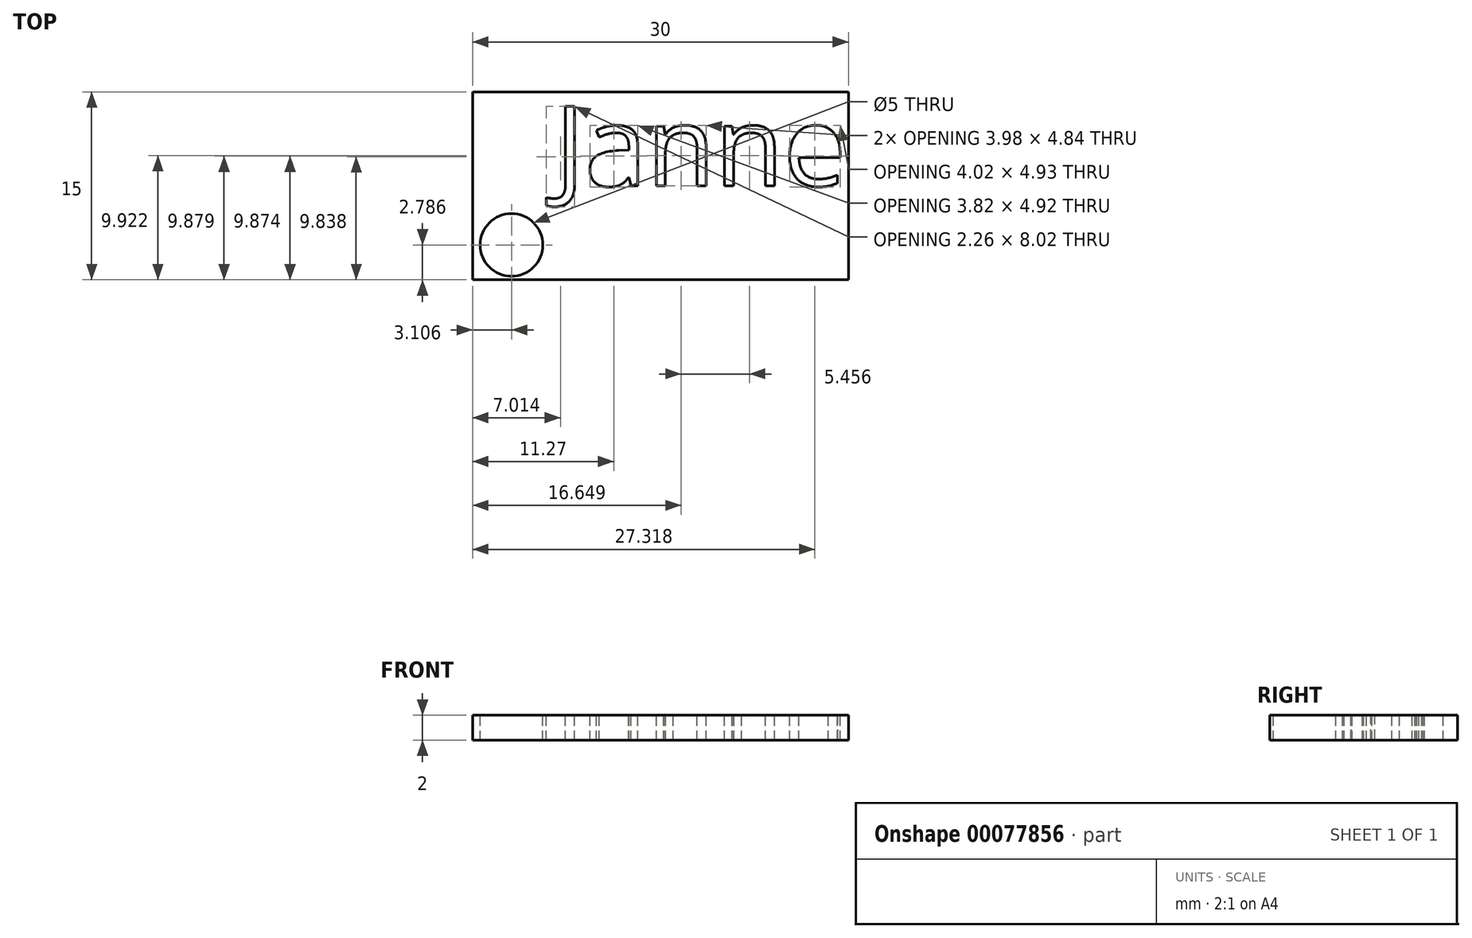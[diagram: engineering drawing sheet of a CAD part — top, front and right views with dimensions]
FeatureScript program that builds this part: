
annotation { "Feature Type Name" : "Feature", "Feature Type Description" : "" }
export const myFeature = defineFeature(function(context is Context, id is Id, definition is map)
    precondition{}
    {
        {
            var Q0;
            Q0=qCreatedBy(makeId("Top.planeOp"),FACE);
            var Q1;
            Q1=qCreatedBy(makeId("Top.planeOp"),FACE);
            var sketch = newSketch(context, id + "F0", { "sketchPlane" : qUnion([Q0, Q1])});
            skLineSegment(sketch, "E0", {"start": v(0, 0) * mm, "end": v(-30, 0) * mm});
            skLineSegment(sketch, "E1", {"start": v(-30, 0) * mm, "end": v(-30, 15) * mm});
            skLineSegment(sketch, "E2", {"start": v(-30, 15) * mm, "end": v(0, 15) * mm});
            skLineSegment(sketch, "E3", {"start": v(0, 15) * mm, "end": v(0, 0) * mm});
            skText(sketch, "E4", { "text": "Janne", "fontName": "OpenSans-Regular.ttf"});
            const initialGuessF0  = {"E4": [-0.02342, 0.0075, 1, 0, 0.0064]};
            skSetInitialGuess(sketch, initialGuessF0);
            skSolve(sketch);
        }
        {
            var Q0;
            Q0=makeQuery(id+"F0.imprint","IMPRINT",FACE,{"disambiguationData":[TD([[makeQuery(id+"F0.imprint","IMPRINT",EDGE,{"derivedFrom":sQuery(id+"F0.wireOp",EDGE,"E0")}),-1.0]])]});
            extrude(context, id + "F1", {"entities" : qUnion([Q0]), "oppositeDirection" : true, "depth" : 2 * mm});
        }
        {
            var Q0;
            Q0=makeQuery(id+"F1.opExtrude","CAP_FACE",FACE,{"disambiguationData":[OSD([sQuery(id+"F0.wireOp",EDGE,"E0"),sQuery(id+"F0.wireOp",EDGE,"E1"),sQuery(id+"F0.wireOp",EDGE,"E2"),sQuery(id+"F0.wireOp",EDGE,"E3"),sQuery(id+"F0.wireOp",EDGE,"E4.sketch_text.stroke-0"),sQuery(id+"F0.wireOp",EDGE,"E4.sketch_text.stroke-1"),sQuery(id+"F0.wireOp",EDGE,"E4.sketch_text.stroke-2"),sQuery(id+"F0.wireOp",EDGE,"E4.sketch_text.stroke-3"),sQuery(id+"F0.wireOp",EDGE,"E4.sketch_text.stroke-4"),sQuery(id+"F0.wireOp",EDGE,"E4.sketch_text.stroke-5"),sQuery(id+"F0.wireOp",EDGE,"E4.sketch_text.stroke-6"),sQuery(id+"F0.wireOp",EDGE,"E4.sketch_text.stroke-7"),sQuery(id+"F0.wireOp",EDGE,"E4.sketch_text.stroke-8"),sQuery(id+"F0.wireOp",EDGE,"E4.sketch_text.stroke-9"),sQuery(id+"F0.wireOp",EDGE,"E4.sketch_text.stroke-10"),sQuery(id+"F0.wireOp",EDGE,"E4.sketch_text.stroke-11"),sQuery(id+"F0.wireOp",EDGE,"E4.sketch_text.stroke-12"),sQuery(id+"F0.wireOp",EDGE,"E4.sketch_text.stroke-13"),sQuery(id+"F0.wireOp",EDGE,"E4.sketch_text.stroke-14"),sQuery(id+"F0.wireOp",EDGE,"E4.sketch_text.stroke-15"),sQuery(id+"F0.wireOp",EDGE,"E4.sketch_text.stroke-16"),sQuery(id+"F0.wireOp",EDGE,"E4.sketch_text.stroke-17"),sQuery(id+"F0.wireOp",EDGE,"E4.sketch_text.stroke-18"),sQuery(id+"F0.wireOp",EDGE,"E4.sketch_text.stroke-19"),sQuery(id+"F0.wireOp",EDGE,"E4.sketch_text.stroke-20"),sQuery(id+"F0.wireOp",EDGE,"E4.sketch_text.stroke-21"),sQuery(id+"F0.wireOp",EDGE,"E4.sketch_text.stroke-22"),sQuery(id+"F0.wireOp",EDGE,"E4.sketch_text.stroke-23"),sQuery(id+"F0.wireOp",EDGE,"E4.sketch_text.stroke-24"),sQuery(id+"F0.wireOp",EDGE,"E4.sketch_text.stroke-25"),sQuery(id+"F0.wireOp",EDGE,"E4.sketch_text.stroke-26"),sQuery(id+"F0.wireOp",EDGE,"E4.sketch_text.stroke-27"),sQuery(id+"F0.wireOp",EDGE,"E4.sketch_text.stroke-28"),sQuery(id+"F0.wireOp",EDGE,"E4.sketch_text.stroke-37"),sQuery(id+"F0.wireOp",EDGE,"E4.sketch_text.stroke-38"),sQuery(id+"F0.wireOp",EDGE,"E4.sketch_text.stroke-39"),sQuery(id+"F0.wireOp",EDGE,"E4.sketch_text.stroke-40"),sQuery(id+"F0.wireOp",EDGE,"E4.sketch_text.stroke-41"),sQuery(id+"F0.wireOp",EDGE,"E4.sketch_text.stroke-42"),sQuery(id+"F0.wireOp",EDGE,"E4.sketch_text.stroke-43"),sQuery(id+"F0.wireOp",EDGE,"E4.sketch_text.stroke-44"),sQuery(id+"F0.wireOp",EDGE,"E4.sketch_text.stroke-45"),sQuery(id+"F0.wireOp",EDGE,"E4.sketch_text.stroke-46"),sQuery(id+"F0.wireOp",EDGE,"E4.sketch_text.stroke-47"),sQuery(id+"F0.wireOp",EDGE,"E4.sketch_text.stroke-48"),sQuery(id+"F0.wireOp",EDGE,"E4.sketch_text.stroke-49"),sQuery(id+"F0.wireOp",EDGE,"E4.sketch_text.stroke-50"),sQuery(id+"F0.wireOp",EDGE,"E4.sketch_text.stroke-51"),sQuery(id+"F0.wireOp",EDGE,"E4.sketch_text.stroke-52"),sQuery(id+"F0.wireOp",EDGE,"E4.sketch_text.stroke-53"),sQuery(id+"F0.wireOp",EDGE,"E4.sketch_text.stroke-54"),sQuery(id+"F0.wireOp",EDGE,"E4.sketch_text.stroke-55"),sQuery(id+"F0.wireOp",EDGE,"E4.sketch_text.stroke-56"),sQuery(id+"F0.wireOp",EDGE,"E4.sketch_text.stroke-57"),sQuery(id+"F0.wireOp",EDGE,"E4.sketch_text.stroke-58"),sQuery(id+"F0.wireOp",EDGE,"E4.sketch_text.stroke-59"),sQuery(id+"F0.wireOp",EDGE,"E4.sketch_text.stroke-60"),sQuery(id+"F0.wireOp",EDGE,"E4.sketch_text.stroke-61"),sQuery(id+"F0.wireOp",EDGE,"E4.sketch_text.stroke-62"),sQuery(id+"F0.wireOp",EDGE,"E4.sketch_text.stroke-63"),sQuery(id+"F0.wireOp",EDGE,"E4.sketch_text.stroke-64"),sQuery(id+"F0.wireOp",EDGE,"E4.sketch_text.stroke-65"),sQuery(id+"F0.wireOp",EDGE,"E4.sketch_text.stroke-66"),sQuery(id+"F0.wireOp",EDGE,"E4.sketch_text.stroke-67"),sQuery(id+"F0.wireOp",EDGE,"E4.sketch_text.stroke-68"),sQuery(id+"F0.wireOp",EDGE,"E4.sketch_text.stroke-69"),sQuery(id+"F0.wireOp",EDGE,"E4.sketch_text.stroke-70"),sQuery(id+"F0.wireOp",EDGE,"E4.sketch_text.stroke-71"),sQuery(id+"F0.wireOp",EDGE,"E4.sketch_text.stroke-72"),sQuery(id+"F0.wireOp",EDGE,"E4.sketch_text.stroke-73"),sQuery(id+"F0.wireOp",EDGE,"E4.sketch_text.stroke-74"),sQuery(id+"F0.wireOp",EDGE,"E4.sketch_text.stroke-75"),sQuery(id+"F0.wireOp",EDGE,"E4.sketch_text.stroke-76"),sQuery(id+"F0.wireOp",EDGE,"E4.sketch_text.stroke-77"),sQuery(id+"F0.wireOp",EDGE,"E4.sketch_text.stroke-78"),sQuery(id+"F0.wireOp",EDGE,"E4.sketch_text.stroke-79"),sQuery(id+"F0.wireOp",EDGE,"E4.sketch_text.stroke-80"),sQuery(id+"F0.wireOp",EDGE,"E4.sketch_text.stroke-81"),sQuery(id+"F0.wireOp",EDGE,"E4.sketch_text.stroke-82"),sQuery(id+"F0.wireOp",EDGE,"E4.sketch_text.stroke-83"),sQuery(id+"F0.wireOp",EDGE,"E4.sketch_text.stroke-84")])],"isStart":true});
            var sketch = newSketch(context, id + "F2", { "sketchPlane" : qUnion([Q0])});
            skPoint(sketch, "E5", {"position": v(-26.9, 2.79) * mm});
            skSolve(sketch);
        }
        {
            var Q0;
            Q0=sQuery(id+"F2.wireOp",VERTEX,"E5");
            var Q1;
            Q1=makeQuery(id+"F1.opExtrude","SWEPT_BODY",BODY,{"disambiguationData":[OSD([sQuery(id+"F0.wireOp",EDGE,"E0"),sQuery(id+"F0.wireOp",EDGE,"E1"),sQuery(id+"F0.wireOp",EDGE,"E2"),sQuery(id+"F0.wireOp",EDGE,"E3"),sQuery(id+"F0.wireOp",EDGE,"E4.sketch_text.stroke-0"),sQuery(id+"F0.wireOp",EDGE,"E4.sketch_text.stroke-1"),sQuery(id+"F0.wireOp",EDGE,"E4.sketch_text.stroke-2"),sQuery(id+"F0.wireOp",EDGE,"E4.sketch_text.stroke-3"),sQuery(id+"F0.wireOp",EDGE,"E4.sketch_text.stroke-4"),sQuery(id+"F0.wireOp",EDGE,"E4.sketch_text.stroke-5"),sQuery(id+"F0.wireOp",EDGE,"E4.sketch_text.stroke-6"),sQuery(id+"F0.wireOp",EDGE,"E4.sketch_text.stroke-7"),sQuery(id+"F0.wireOp",EDGE,"E4.sketch_text.stroke-8"),sQuery(id+"F0.wireOp",EDGE,"E4.sketch_text.stroke-9"),sQuery(id+"F0.wireOp",EDGE,"E4.sketch_text.stroke-10"),sQuery(id+"F0.wireOp",EDGE,"E4.sketch_text.stroke-11"),sQuery(id+"F0.wireOp",EDGE,"E4.sketch_text.stroke-12"),sQuery(id+"F0.wireOp",EDGE,"E4.sketch_text.stroke-13"),sQuery(id+"F0.wireOp",EDGE,"E4.sketch_text.stroke-14"),sQuery(id+"F0.wireOp",EDGE,"E4.sketch_text.stroke-15"),sQuery(id+"F0.wireOp",EDGE,"E4.sketch_text.stroke-16"),sQuery(id+"F0.wireOp",EDGE,"E4.sketch_text.stroke-17"),sQuery(id+"F0.wireOp",EDGE,"E4.sketch_text.stroke-18"),sQuery(id+"F0.wireOp",EDGE,"E4.sketch_text.stroke-19"),sQuery(id+"F0.wireOp",EDGE,"E4.sketch_text.stroke-20"),sQuery(id+"F0.wireOp",EDGE,"E4.sketch_text.stroke-21"),sQuery(id+"F0.wireOp",EDGE,"E4.sketch_text.stroke-22"),sQuery(id+"F0.wireOp",EDGE,"E4.sketch_text.stroke-23"),sQuery(id+"F0.wireOp",EDGE,"E4.sketch_text.stroke-24"),sQuery(id+"F0.wireOp",EDGE,"E4.sketch_text.stroke-25"),sQuery(id+"F0.wireOp",EDGE,"E4.sketch_text.stroke-26"),sQuery(id+"F0.wireOp",EDGE,"E4.sketch_text.stroke-27"),sQuery(id+"F0.wireOp",EDGE,"E4.sketch_text.stroke-28"),sQuery(id+"F0.wireOp",EDGE,"E4.sketch_text.stroke-37"),sQuery(id+"F0.wireOp",EDGE,"E4.sketch_text.stroke-38"),sQuery(id+"F0.wireOp",EDGE,"E4.sketch_text.stroke-39"),sQuery(id+"F0.wireOp",EDGE,"E4.sketch_text.stroke-40"),sQuery(id+"F0.wireOp",EDGE,"E4.sketch_text.stroke-41"),sQuery(id+"F0.wireOp",EDGE,"E4.sketch_text.stroke-42"),sQuery(id+"F0.wireOp",EDGE,"E4.sketch_text.stroke-43"),sQuery(id+"F0.wireOp",EDGE,"E4.sketch_text.stroke-44"),sQuery(id+"F0.wireOp",EDGE,"E4.sketch_text.stroke-45"),sQuery(id+"F0.wireOp",EDGE,"E4.sketch_text.stroke-46"),sQuery(id+"F0.wireOp",EDGE,"E4.sketch_text.stroke-47"),sQuery(id+"F0.wireOp",EDGE,"E4.sketch_text.stroke-48"),sQuery(id+"F0.wireOp",EDGE,"E4.sketch_text.stroke-49"),sQuery(id+"F0.wireOp",EDGE,"E4.sketch_text.stroke-50"),sQuery(id+"F0.wireOp",EDGE,"E4.sketch_text.stroke-51"),sQuery(id+"F0.wireOp",EDGE,"E4.sketch_text.stroke-52"),sQuery(id+"F0.wireOp",EDGE,"E4.sketch_text.stroke-53"),sQuery(id+"F0.wireOp",EDGE,"E4.sketch_text.stroke-54"),sQuery(id+"F0.wireOp",EDGE,"E4.sketch_text.stroke-55"),sQuery(id+"F0.wireOp",EDGE,"E4.sketch_text.stroke-56"),sQuery(id+"F0.wireOp",EDGE,"E4.sketch_text.stroke-57"),sQuery(id+"F0.wireOp",EDGE,"E4.sketch_text.stroke-58"),sQuery(id+"F0.wireOp",EDGE,"E4.sketch_text.stroke-59"),sQuery(id+"F0.wireOp",EDGE,"E4.sketch_text.stroke-60"),sQuery(id+"F0.wireOp",EDGE,"E4.sketch_text.stroke-61"),sQuery(id+"F0.wireOp",EDGE,"E4.sketch_text.stroke-62"),sQuery(id+"F0.wireOp",EDGE,"E4.sketch_text.stroke-63"),sQuery(id+"F0.wireOp",EDGE,"E4.sketch_text.stroke-64"),sQuery(id+"F0.wireOp",EDGE,"E4.sketch_text.stroke-65"),sQuery(id+"F0.wireOp",EDGE,"E4.sketch_text.stroke-66"),sQuery(id+"F0.wireOp",EDGE,"E4.sketch_text.stroke-67"),sQuery(id+"F0.wireOp",EDGE,"E4.sketch_text.stroke-68"),sQuery(id+"F0.wireOp",EDGE,"E4.sketch_text.stroke-69"),sQuery(id+"F0.wireOp",EDGE,"E4.sketch_text.stroke-70"),sQuery(id+"F0.wireOp",EDGE,"E4.sketch_text.stroke-71"),sQuery(id+"F0.wireOp",EDGE,"E4.sketch_text.stroke-72"),sQuery(id+"F0.wireOp",EDGE,"E4.sketch_text.stroke-73"),sQuery(id+"F0.wireOp",EDGE,"E4.sketch_text.stroke-74"),sQuery(id+"F0.wireOp",EDGE,"E4.sketch_text.stroke-75"),sQuery(id+"F0.wireOp",EDGE,"E4.sketch_text.stroke-76"),sQuery(id+"F0.wireOp",EDGE,"E4.sketch_text.stroke-77"),sQuery(id+"F0.wireOp",EDGE,"E4.sketch_text.stroke-78"),sQuery(id+"F0.wireOp",EDGE,"E4.sketch_text.stroke-79"),sQuery(id+"F0.wireOp",EDGE,"E4.sketch_text.stroke-80"),sQuery(id+"F0.wireOp",EDGE,"E4.sketch_text.stroke-81"),sQuery(id+"F0.wireOp",EDGE,"E4.sketch_text.stroke-82"),sQuery(id+"F0.wireOp",EDGE,"E4.sketch_text.stroke-83"),sQuery(id+"F0.wireOp",EDGE,"E4.sketch_text.stroke-84")])]});
            hole(context, id + "F3", {"style" : HoleStyle.SIMPLE, "endStyle" : HoleEndStyle.BLIND, "holeDiameter" : 5 * mm, "holeDepth" : 2 * mm, "locations" : qUnion([Q0]), "scope" : qUnion([Q1])});
        }
    });
